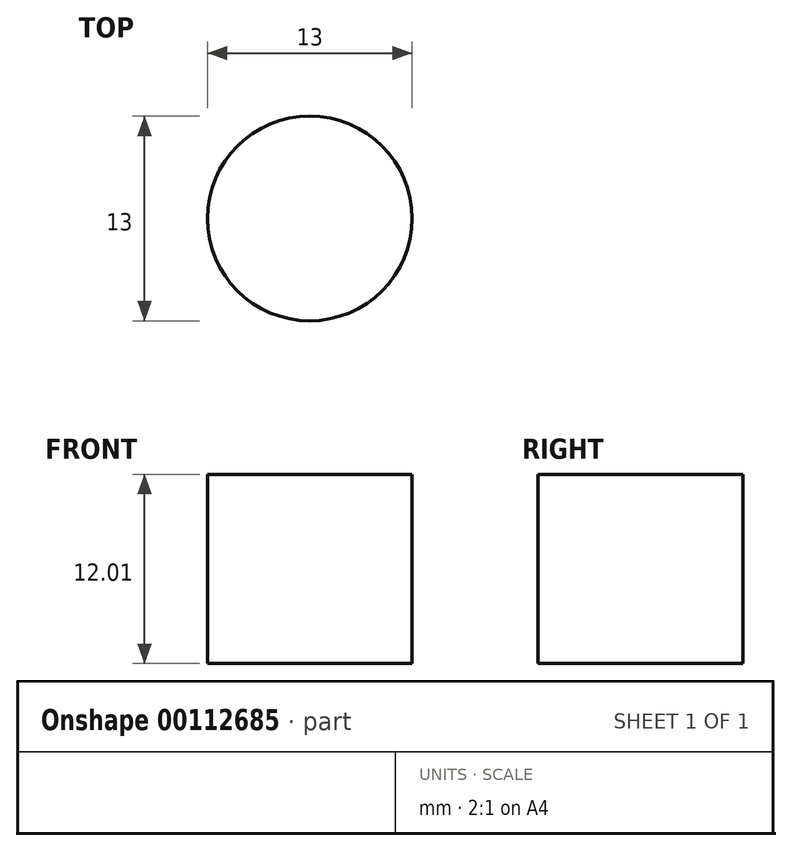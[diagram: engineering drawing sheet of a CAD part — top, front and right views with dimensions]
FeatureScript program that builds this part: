
annotation { "Feature Type Name" : "Feature", "Feature Type Description" : "" }
export const myFeature = defineFeature(function(context is Context, id is Id, definition is map)
    precondition{}
    {
        {
            var Q0;
            Q0=qCreatedBy(makeId("Top.planeOp"),FACE);
            var sketch = newSketch(context, id + "F0", { "sketchPlane" : qUnion([Q0])});
            skCircle(sketch, "E0", {"center": v(0, 0) * mm, "radius": 6.5 * mm});
            skSolve(sketch);
        }
        {
            var Q0;
            Q0 = qSketchRegion(id + "F0", true);
            extrude(context, id + "F1", {"entities" : qUnion([Q0]), "depth" : 12 * mm});
        }
    });
